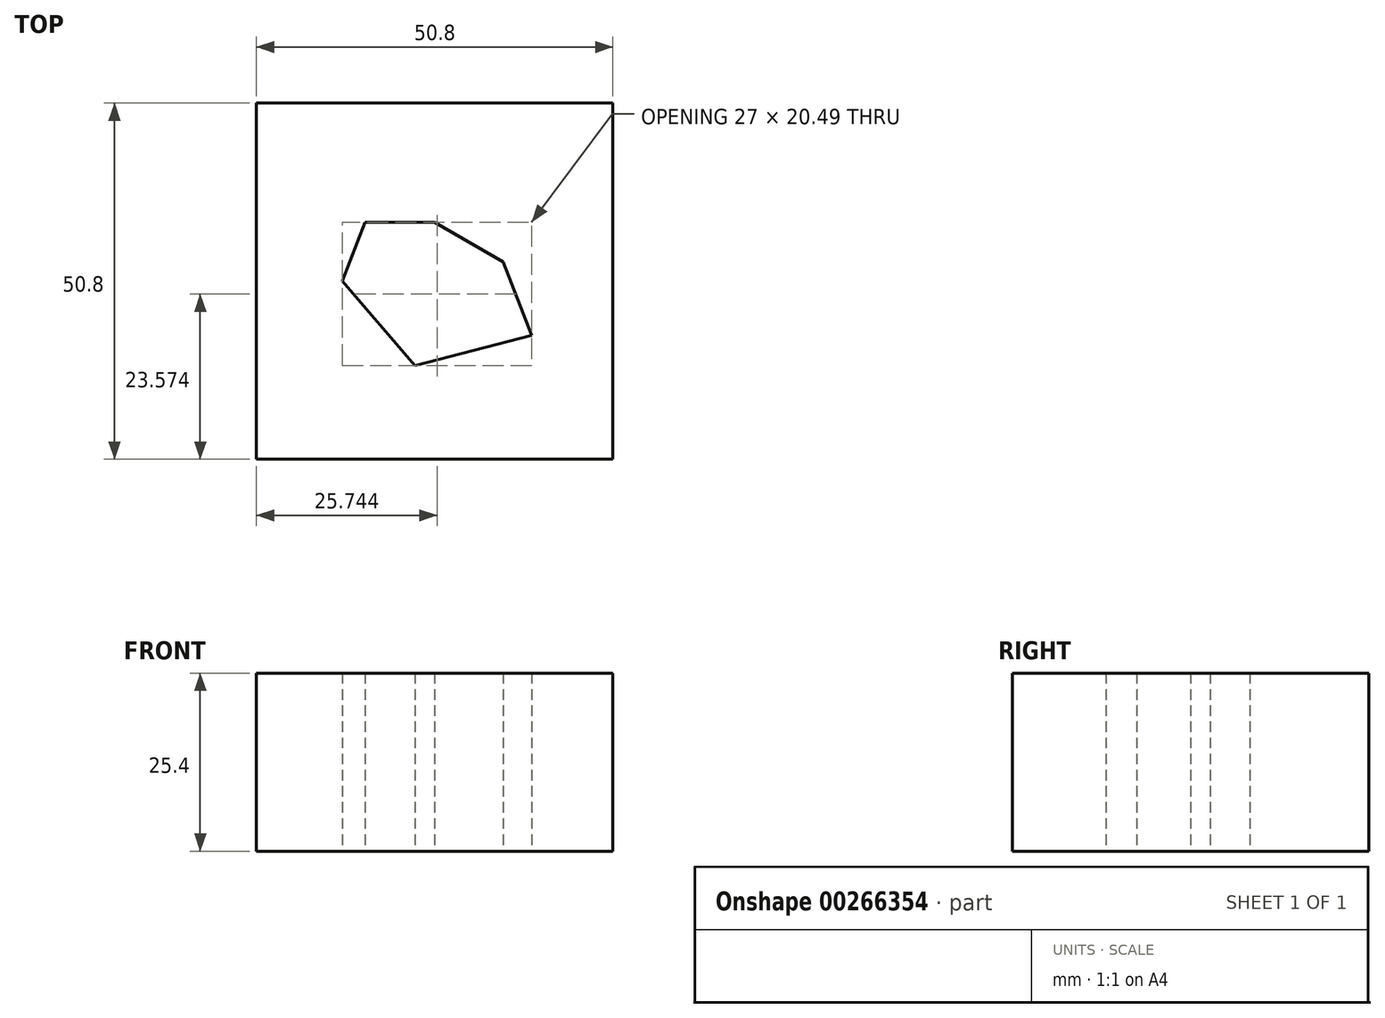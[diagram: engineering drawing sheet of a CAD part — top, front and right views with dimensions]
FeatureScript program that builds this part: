
annotation { "Feature Type Name" : "Feature", "Feature Type Description" : "" }
export const myFeature = defineFeature(function(context is Context, id is Id, definition is map)
    precondition{}
    {
        {
            var Q0;
            Q0=qCreatedBy(makeId("Top.planeOp"),FACE);
            var sketch = newSketch(context, id + "F0", { "sketchPlane" : qUnion([Q0])});
            skLineSegment(sketch, "E0.bottom", {"start": v(25.4, 25.4) * mm, "end": v(-25.4, 25.4) * mm});
            skLineSegment(sketch, "E0.top", {"start": v(25.4, -25.4) * mm, "end": v(-25.4, -25.4) * mm});
            skLineSegment(sketch, "E0.left", {"start": v(25.4, 25.4) * mm, "end": v(25.4, -25.4) * mm});
            skLineSegment(sketch, "E0.right", {"start": v(-25.4, 25.4) * mm, "end": v(-25.4, -25.4) * mm});
            skPoint(sketch, "E0.middle", {"position": v(0, 0) * mm});
            skCircle(sketch, "E1", {"center": v(0, 0) * mm, "radius": 22.23 * mm});
            skLineSegment(sketch, "E2", {"start": v(-13.16, 0) * mm, "end": v(-9.9, 8.42) * mm});
            skLineSegment(sketch, "E3", {"start": v(-9.9, 8.42) * mm, "end": v(0, 8.42) * mm});
            skLineSegment(sketch, "E4", {"start": v(9.75, 2.75) * mm, "end": v(0, 8.42) * mm});
            skLineSegment(sketch, "E5", {"start": v(9.75, 2.75) * mm, "end": v(13.84, -7.73) * mm});
            skLineSegment(sketch, "E6", {"start": v(13.84, -7.73) * mm, "end": v(-2.8, -12.07) * mm});
            skLineSegment(sketch, "E7", {"start": v(-2.8, -12.07) * mm, "end": v(-13.16, 0) * mm});
            skSolve(sketch);
        }
        {
            var Q0;
            Q0=makeQuery(id+"F0.imprint","IMPRINT",FACE,{"disambiguationData":[TD([[makeQuery(id+"F0.imprint","IMPRINT",EDGE,{"derivedFrom":sQuery(id+"F0.wireOp",EDGE,"E1")}),1.0]])]});
            var Q1;
            Q1=makeQuery(id+"F0.imprint","IMPRINT",FACE,{"disambiguationData":[TD([[makeQuery(id+"F0.imprint","IMPRINT",EDGE,{"derivedFrom":sQuery(id+"F0.wireOp",EDGE,"E0.bottom")}),1.0]])]});
            extrude(context, id + "F1", {"entities" : qUnion([Q0, Q1]), "depth" : 25.4 * mm});
        }
    });
